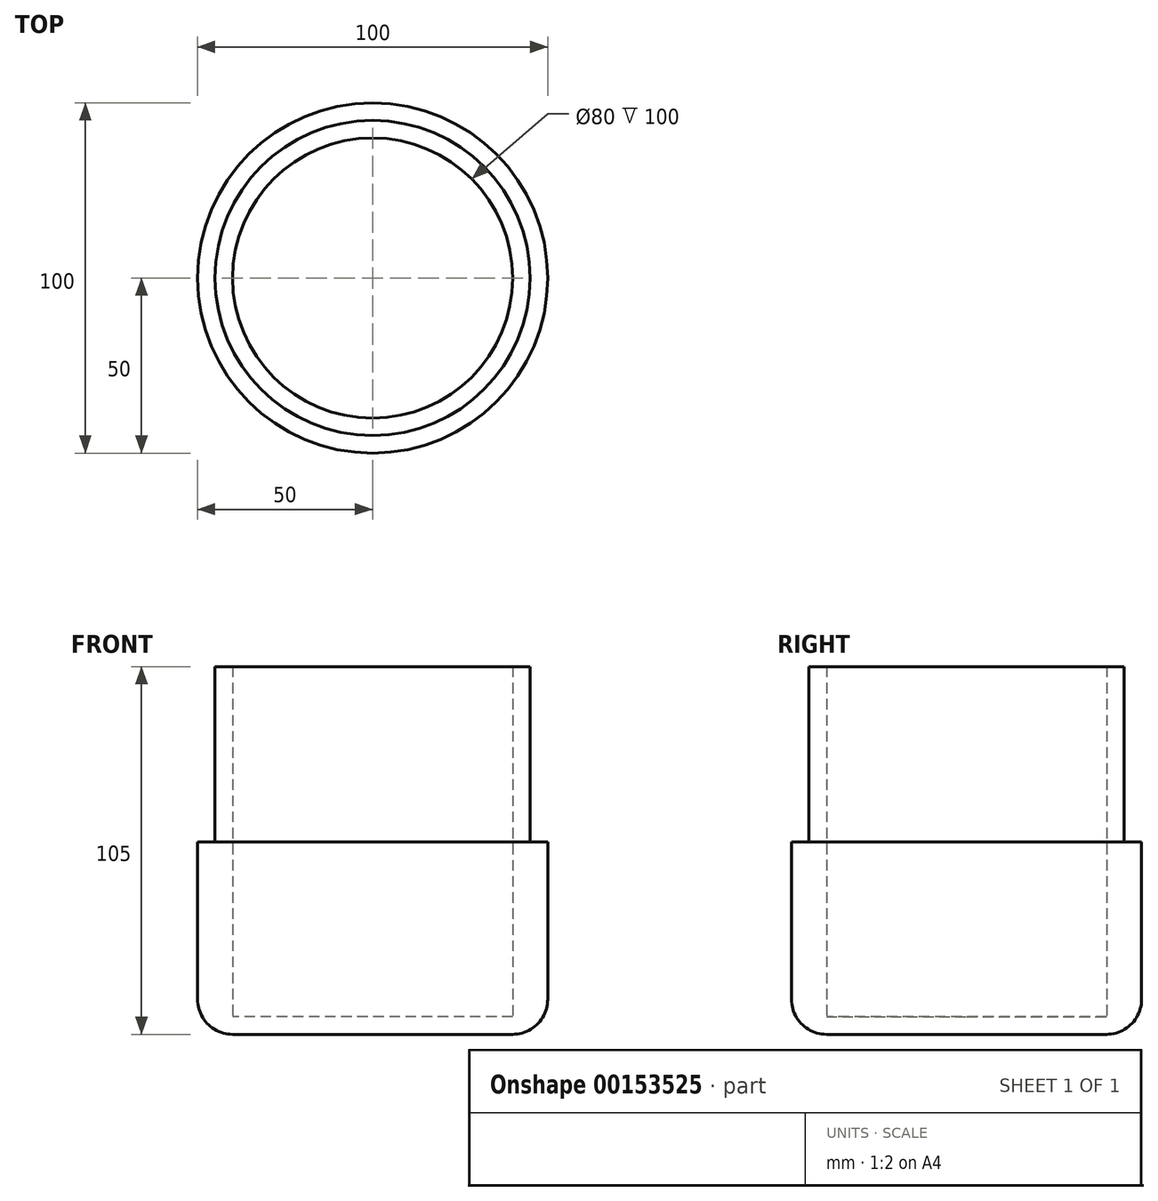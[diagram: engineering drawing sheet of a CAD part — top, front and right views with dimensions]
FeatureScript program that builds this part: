
annotation { "Feature Type Name" : "Feature", "Feature Type Description" : "" }
export const myFeature = defineFeature(function(context is Context, id is Id, definition is map)
    precondition{}
    {
        {
            var Q0;
            Q0=qCreatedBy(makeId("Top.planeOp"),FACE);
            var sketch = newSketch(context, id + "F0", { "sketchPlane" : qUnion([Q0])});
            skCircle(sketch, "E0", {"center": v(0, 0) * mm, "radius": 40 * mm});
            skCircle(sketch, "E1", {"center": v(0, 0) * mm, "radius": 45 * mm});
            skCircle(sketch, "E2", {"center": v(0, 0) * mm, "radius": 50 * mm});
            skSolve(sketch);
        }
        {
            var Q0;
            Q0 = qSketchRegion(id + "F0", true);
            extrude(context, id + "F1", {"entities" : qUnion([Q0]), "depth" : 50 * mm});
        }
        {
            var Q0;
            Q0=makeQuery(id+"F0.imprint","IMPRINT",FACE,{"disambiguationData":[TD([[makeQuery(id+"F0.imprint","IMPRINT",EDGE,{"derivedFrom":sQuery(id+"F0.wireOp",EDGE,"E0")}),-1.0]])]});
            extrude(context, id + "F2", {"entities" : qUnion([Q0]), "operationType" : NewBodyOperationType.ADD, "depth" : 100 * mm});
        }
        {
            var Q0;
            Q0=makeQuery(id+"F0.imprint","IMPRINT",FACE,{"disambiguationData":[TD([[makeQuery(id+"F0.imprint","IMPRINT",EDGE,{"derivedFrom":sQuery(id+"F0.wireOp",EDGE,"E1")}),-1.0]])]});
            var Q1;
            Q1=makeQuery(id+"F0.imprint","IMPRINT",FACE,{"disambiguationData":[TD([[makeQuery(id+"F0.imprint","IMPRINT",EDGE,{"derivedFrom":sQuery(id+"F0.wireOp",EDGE,"E0")}),-1.0]])]});
            var Q2;
            Q2=makeQuery(id+"F0.imprint","IMPRINT",FACE,{"disambiguationData":[TD([[makeQuery(id+"F0.imprint","IMPRINT",EDGE,{"derivedFrom":sQuery(id+"F0.wireOp",EDGE,"E0")}),1.0]])]});
            extrude(context, id + "F3", {"entities" : qUnion([Q0, Q1, Q2]), "operationType" : NewBodyOperationType.ADD, "oppositeDirection" : true, "depth" : 5 * mm});
        }
        {
            var Q0;
            Q0=makeQuery(id+"F3.opExtrude","CAP_EDGE",EDGE,{"disambiguationData":[OSD([sQuery(id+"F0.wireOp",EDGE,"E2")])],"isStart":false});
            fillet(context, id + "F4", {"entities" : qUnion([Q0]), "radius" : 10 * mm, "tangentPropagation" : true, "allowEdgeOverflow" : false});
        }
    });
